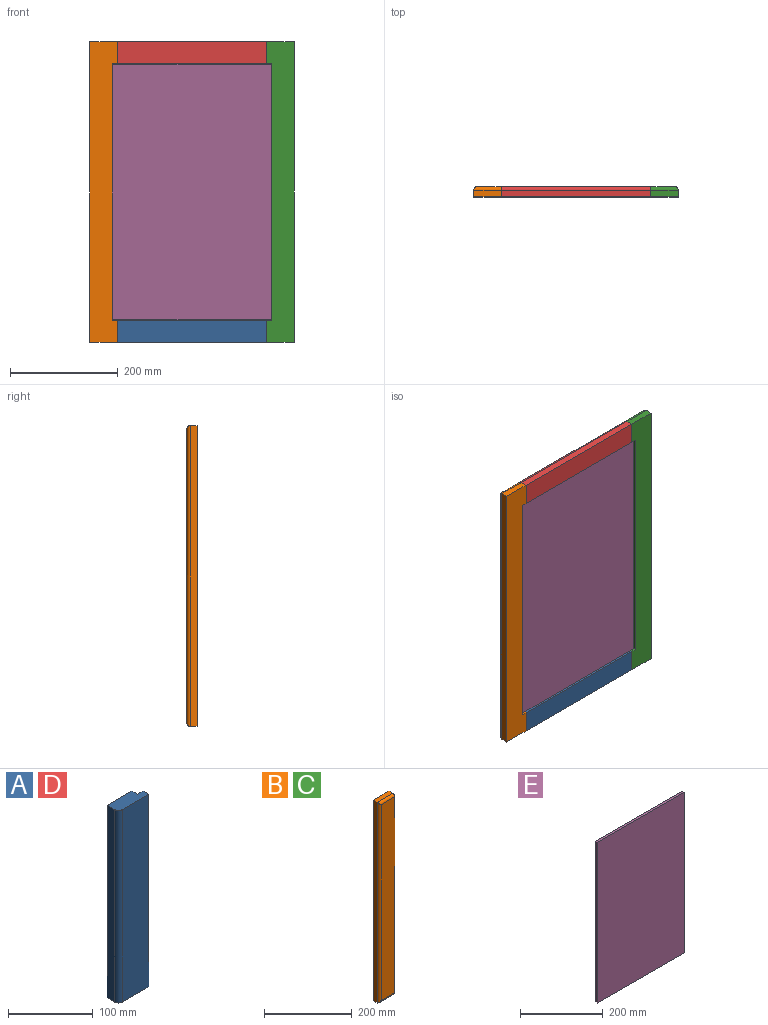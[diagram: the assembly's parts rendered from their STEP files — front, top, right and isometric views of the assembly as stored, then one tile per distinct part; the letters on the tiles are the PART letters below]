
ASSEMBLY  parts=5 mates=4
PART A: 9 faces, bbox 50.8x19.1x277.8 mm
  f0: plane 50.8x19.05mm, normal (0,0,1), area 868.4mm2, adj f2,f3,f4,f5,f6,f7,f8
  f1: plane 50.8x19.05mm, normal (0,0,-1), area 868.4mm2, adj f2,f3,f4,f5,f6,f7,f8
  f2: plane 277.81x12.7mm, normal (-1,0,0), area 3528.2mm2, adj f0,f1,f5,f6
  f3: plane 277.81x44.45mm, normal (0,-1,0), area 12348.8mm2, adj f0,f1,f4,f6
  f4: plane 277.81x9.53mm, normal (1,0,0), area 2646.2mm2, adj f0,f1,f3,f7
  f5: plane 277.81x41.28mm, normal (0,1,0), area 11466.7mm2, adj f0,f1,f2,f8
  f6: cylinder r=6.35mm len=277.81mm, axis (0,0,1), area 2771.1mm2, adj f0,f1,f2,f3
  f7: plane 277.81x9.53mm, normal (0,1,0), area 2646.2mm2, adj f0,f1,f4,f8
  f8: plane 277.81x9.53mm, normal (1,0,0), area 2646.2mm2, adj f0,f1,f5,f7
PART B: 13 faces, bbox 50.8x19.1x558.8 mm
  f0: plane 558.8x19.05mm, normal (1,0,0), area 6091.6mm2, adj f1,f3,f4,f5,f6,f7,f9,f10
  f1: plane 558.8x50.8mm, normal (0,1,0), area 23850.8mm2, adj f0,f2,f4,f5,f9,f10,f11
  f2: plane 558.8x12.7mm, normal (-1,0,0), area 7096.8mm2, adj f1,f4,f5,f8
  f3: plane 546.1x44.45mm, normal (0,-1,0), area 24274.1mm2, adj f0,f6,f7,f8
  f4: plane 50.8x12.7mm, normal (0,0,1), area 645.2mm2, adj f0,f1,f2,f6
  f5: plane 50.8x12.7mm, normal (0,0,-1), area 645.2mm2, adj f0,f1,f2,f7
  f6: cylinder r=6.35mm len=50.8mm, axis (-1,0,0), area 483.7mm2, adj f0,f3,f4,f8
  f7: cylinder r=6.35mm len=50.8mm, axis (1,0,0), area 483.7mm2, adj f0,f3,f5,f8
  f8: cylinder r=6.35mm len=558.8mm, axis (0,0,1), area 5527.8mm2, adj f2,f3,f6,f7
  f9: plane 9.53x9.53mm, normal (0,0,1), area 90.7mm2, adj f0,f1,f11,f12
  f10: plane 9.53x9.53mm, normal (0,0,-1), area 90.7mm2, adj f0,f1,f11,f12
  f11: plane 476.25x9.53mm, normal (1,0,0), area 4536.3mm2, adj f1,f9,f10,f12
  f12: plane 476.25x9.53mm, normal (0,1,0), area 4536.3mm2, adj f0,f9,f10,f11
PART C: same geometry as B
PART D: same geometry as A
PART E: 6 faces, bbox 296.9x6.4x474.7 mm
  f0: plane 474.66x6.35mm, normal (-1,0,0), area 3014.1mm2, adj f1,f3,f4,f5
  f1: plane 296.86x6.35mm, normal (0,0,-1), area 1885.1mm2, adj f0,f2,f4,f5
  f2: plane 474.66x6.35mm, normal (1,0,0), area 3014.1mm2, adj f1,f3,f4,f5
  f3: plane 296.86x6.35mm, normal (0,0,1), area 1885.1mm2, adj f0,f2,f4,f5
  f4: plane 474.66x296.86mm, normal (0,-1,0), area 140909.5mm2, adj f0,f1,f2,f3
  f5: plane 474.66x296.86mm, normal (0,1,0), area 140909.5mm2, adj f0,f1,f2,f3
PLACE A rot(axis=(-0.71,0,-0.71),180deg) t=(-300.04,0,-279.4)mm
PLACE B rot(axis=(-1,0,0),180deg) t=(-350.84,0,279.4)mm
PLACE C rot(axis=(0,0,1),180deg) t=(28.58,0,-279.4)mm
PLACE D rot(axis=(-0.71,0,0.71),180deg) t=(-22.23,0,279.4)mm
PLACE E rot(axis=(0,0,1),180deg) t=(-13.49,-15.88,-237.33)mm
MATE fastened C.f4 <-> D.f2  axis (0,0,1) through (-22.23,-12.7,279.4)mm
MATE fastened D.f0 <-> B.f0  axis (-1,0,0) through (-300.04,-19.05,279.4)mm
MATE fastened B.f0 <-> A.f1  axis (1,0,0) through (-300.04,-19.05,-279.4)mm
MATE fastened E.f4 <-> C.f12  axis (0,1,0) through (-13.49,-9.53,237.33)mm
